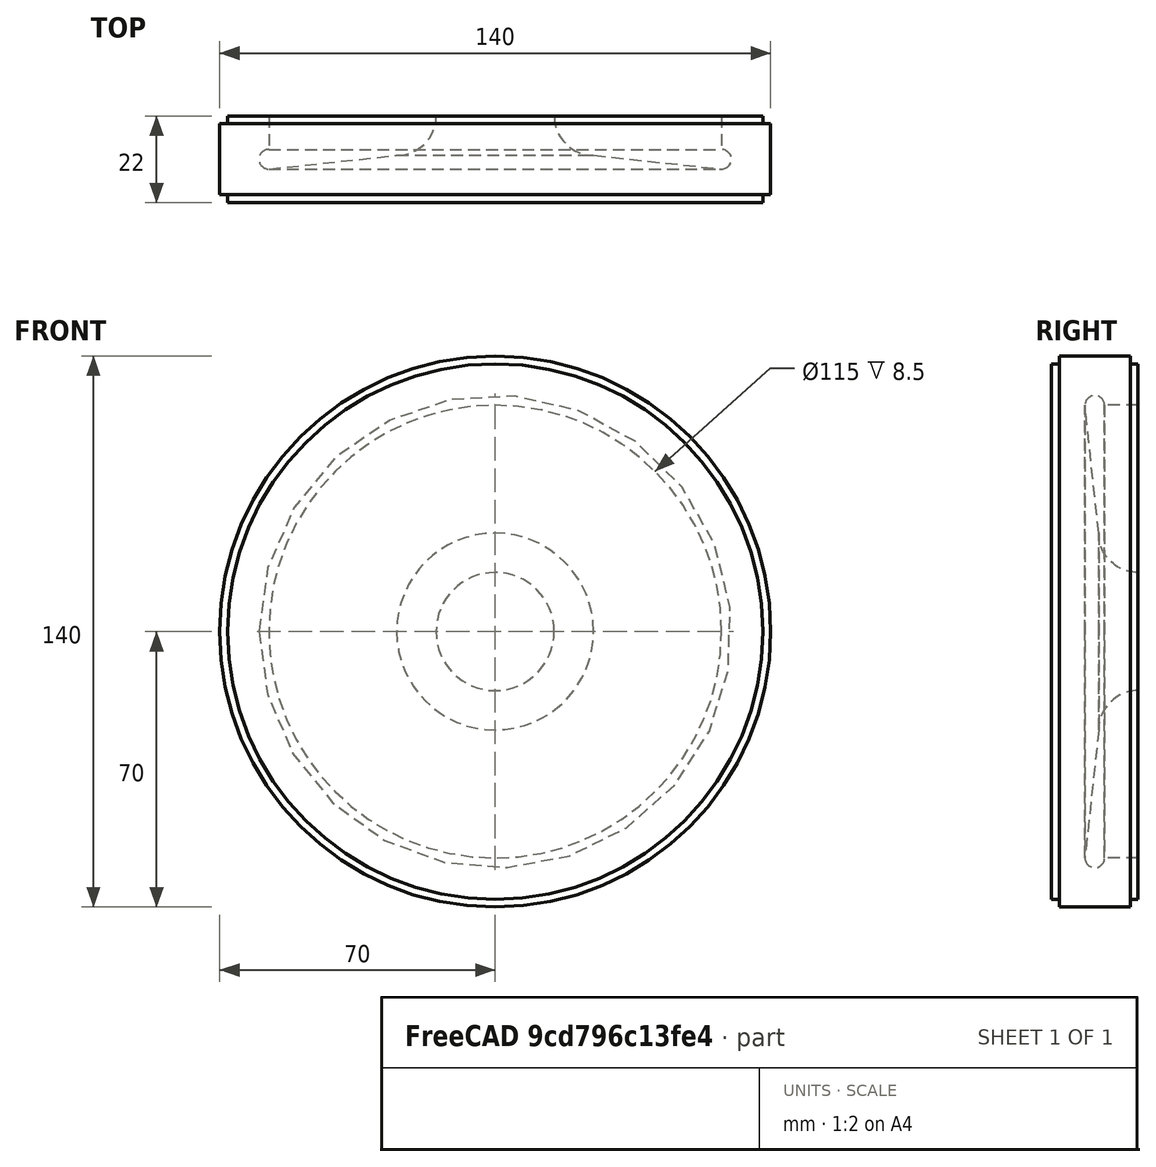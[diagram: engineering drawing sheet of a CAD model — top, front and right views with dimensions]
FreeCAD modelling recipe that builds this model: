
FCSTD DOCUMENT  (FreeCAD 0.18.4R)
Label: блин001
License: All rights reserved
LicenseURL: http://en.wikipedia.org/wiki/All_rights_reserved
objects: TechDraw::DrawViewPart×2, Sketcher::SketchObject×1, PartDesign::Revolution×1, PartDesign::Body×1, TechDraw::DrawSVGTemplate×1, TechDraw::DrawViewSection×1, TechDraw::DrawPage×1
note: 4 computed .brp shape members not serialized (recipe doc carries the construction recipe); baked Part::Feature solids carry a one-line shape summary decoded from their .brp

FEATURE [Sketcher::SketchObject] Sketch
  MapMode = 5
  Support = -> [XY_Plane]
  sketch-geometry (13):
    g0: LineSegment StartX=-68 StartY=22 StartZ=0 EndX=-68 EndY=20 EndZ=0
    g1: LineSegment StartX=-70 StartY=20 StartZ=0 EndX=-68 EndY=20 EndZ=0
    g2: LineSegment StartX=-70 StartY=20 StartZ=0 EndX=-70 EndY=2 EndZ=0
    g3: LineSegment StartX=-70 StartY=2 StartZ=0 EndX=-68 EndY=2 EndZ=0
    g4: LineSegment StartX=-68 StartY=2 StartZ=0 EndX=-68 EndY=0 EndZ=0
    g5: LineSegment StartX=-68 StartY=0 StartZ=0 EndX=0 EndY=0 EndZ=0
    g6: LineSegment StartX=0 StartY=0 StartZ=0 EndX=0 EndY=22 EndZ=0
    g7: LineSegment StartX=0 StartY=22 StartZ=0 EndX=-15 EndY=22 EndZ=0
    g8: LineSegment StartX=-57.5 StartY=8.5 StartZ=0 EndX=-25 EndY=12 EndZ=0
    g9: LineSegment StartX=-68 StartY=22 StartZ=0 EndX=-57.5 EndY=22 EndZ=0
    g10: LineSegment StartX=-57.5 StartY=22 StartZ=0 EndX=-57.5 EndY=13.5 EndZ=0
    g11: ArcOfCircle CenterX=-57.5 CenterY=11 CenterZ=0 NormalX=0 NormalY=0 NormalZ=1 AngleXU=0 Radius=2.5 StartAngle=1.5708 EndAngle=4.71239
    g12: ArcOfCircle CenterX=-25 CenterY=22 CenterZ=0 NormalX=0 NormalY=0 NormalZ=1 AngleXU=0 Radius=10 StartAngle=4.71239 EndAngle=6.28319
  constraints (49):
    c: Vertical(g0)
    c: Vertical(g2)
    c: Vertical(g4)
    c: Coincident(g6,g5)
    c: Vertical(g6)
    c: Coincident(g7,g6)
    c: Horizontal(g7)
    c: Distance(g7) = 15
    c: Distance(g6) = 22
    c: Distance(g5) = 68
    c: Distance(g3) = 2
    c: Distance(g1) = 2
    c: Distance(g8,g2) = 12.5
    c: Distance(g8,g6) = 25
    c: Distance(g9) = 10.5
    c: Vertical(g10)
    c: Distance(g8,g5) = 8.5
    c: Distance(g8,g5) = 12
    c: Coincident(g11,g10)
    c: Coincident(g12,g7)
    c: Coincident(g12,g8)
    c: Radius(g12) = 10
    c: Radius(g11) = 2.5
    c: Distance(g11,g2) = 12.5
    c: DistanceX(g4,g5) = 68
    c: DistanceX(g3,g4) = 0
    c: DistanceX(g2,g3) = 0
    c: DistanceX(g1,g2) = 0
    c: DistanceX(g0,g1) = 0
    c: DistanceX(g9,g0) = 0
    c: DistanceX(g10,g9) = 0
    c: Distance(g2) = 18
    c: DistanceY(g10,g9) = 0
    c: DistanceY(g0,g9) = 0
    c: Perpendicular(g10,g9)
    c: DistanceY(g2,g1) = 0
    c: Perpendicular(g2,g1)
    c: DistanceY(g2,g3) = 0
    c: Perpendicular(g3,g2)
    c: DistanceY(g3,g4) = 0
    c: DistanceY(g5,g4) = 0
    c: Perpendicular(g4,g5)
    c: DistanceX(g11,g8) = 0
    c: DistanceY(g8,g11) = 0
    c: Distance(g4) = 2
    c: Distance(g0) = 2
    c: DistanceY(g1,g0) = 0
    c: PointOnObject(g6,g-2)
    c: PointOnObject(g5,g-1)
FEATURE [PartDesign::Revolution] Revolution
  Angle = 360
  Axis = (0,1,0)
  Base = (0,0,0)
  Profile = -> Sketch
  ReferenceAxis = -> Sketch [V_Axis]
FEATURE [PartDesign::Body] Body
  Group = -> [Sketch,Revolution]
  Origin = -> Origin
  Tip = -> Revolution
FEATURE [TechDraw::DrawSVGTemplate] Template
  EditableTexts = AUTHOR_NAME=AUTHOR NAME; DN=DN; DRAWING_TITLE=DRAWING TITLE; FC-DATE=DD/MM/YYYY; FC-REV=REV A; FC-SC=SCALE; FC-SH=X / Y; FC-SI=A4; FreeCAD_DRAWING=FreeCAD DRAWING; PN=PN
  Height = 297
  Orientation = 0
  Width = 210
FEATURE [TechDraw::DrawViewPart] View
  CoarseView = false
  Direction = (0,0,1)
  Focus = 100
  HardHidden = false
  IsoCount = 0
  IsoHidden = false
  IsoVisible = false
  LockPosition = false
  Perspective = false
  Rotation = 0
  ScaleType = 0
  SeamHidden = false
  SeamVisible = false
  SmoothHidden = false
  SmoothVisible = false
  Source = -> [Revolution]
  X = 106.242
  Y = 271.502
FEATURE [TechDraw::DrawViewPart] View001
  CoarseView = false
  Direction = (0,1,0)
  Focus = 100
  HardHidden = false
  IsoCount = 0
  IsoHidden = false
  IsoVisible = false
  LockPosition = false
  Perspective = false
  Rotation = 0
  ScaleType = 0
  SeamHidden = false
  SeamVisible = false
  SmoothHidden = false
  SmoothVisible = false
  Source = -> [Revolution]
  X = 106.466
  Y = 178.177
FEATURE [TechDraw::DrawViewSection] Section  label="Section A - A"
  BaseView = -> View001
  CoarseView = false
  Direction = (0,0,1)
  Focus = 100
  FuseBeforeCut = true
  HardHidden = false
  HatchScale = 1
  IsoCount = 0
  IsoHidden = false
  IsoVisible = false
  LockPosition = false
  NameGeomPattern = Diamond
  Perspective = false
  Rotation = 0
  ScaleType = 0
  SeamHidden = false
  SeamVisible = false
  SectionDirection = 3
  SectionNormal = (0,0,1)
  SectionOrigin = (0,11,0)
  SectionSymbol = A
  SmoothHidden = false
  SmoothVisible = false
  Source = -> [Revolution]
  X = 106.832
  Y = 84.7495
FEATURE [TechDraw::DrawPage] Page
  KeepUpdated = true
  ProjectionType = 0
  Template = -> Template
  Views = -> [View,View001,Section]
